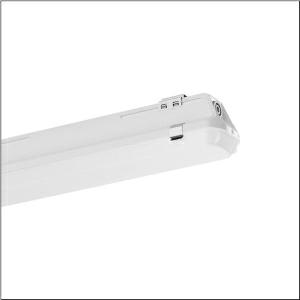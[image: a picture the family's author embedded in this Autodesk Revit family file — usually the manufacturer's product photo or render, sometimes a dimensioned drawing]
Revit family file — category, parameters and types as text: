
# Revit family: monsun_r__21_parking_51fg20dp440bhq_097c
name_source: partatom
category: Lighting Fixtures
units: mm (PartAtom-declared; Revit-internal decimal feet)

## family parameters
Cut with Voids When Loaded = No
Host = Face
Light Source = No
Part Type = Normal
Room Calculation Point = No
Round Connector Dimension = Use Diameter
Shared = No

## types (1)
- --- (1 x LED, 4810 lm, 34.9 W, 4000K)
    Apparent Load = 35 VA
    CIE Flux Codes = 45 75 93 94 100
    Color Rendering = 80
    Color Temperature = 4000K
    Default Elevation = 1800 mm
    Description = Monsun® 21 parking, damp-proof luminaire, chain hanger, primary optical cover: enclosure, of PC, light emission: direct distribution, primary light characteristic: symmetric, installation type: suspended mounting, surface-mounted, horizontal mounting, vertical mounting, LED, rated luminous flux: 4.810lm, luminous efficacy: 140lm/W, light colour: 840, colour temperature: 4000K, control gear: ECG DALI, with terminal, 5-pole, max. 2.5mm², mains connection: 220..240V, AC, 50/60Hz, rated input power: 34W, housing, of glass-fibre reinforced polyester, uncoated, bright grey, incl. chain hanger, length: 1.590mm, width: 90mm, height: 88mm, clip for enclosure, of stainless steel (V2A), ceiling mounting element, of stainless steel (V2A), chain hanger, of stainless steel (V2A), multi-sensor HC1, local controlcentral control, scope of services: certified according to part 101,103,303,304, dimmable, protection rating (complete): IP66, insulation class (complete): insulation class I (protective earthing), certification: CE, ENEC, VDE, UKCA, protection symbol: D, impact resistance: IK08, permissible operating ambient temperature: -25..+35°C, standard: EN 50419, EN 60598-2-1, corresponds to IFS (International Featured Standards) requirements for safety and quality in the food industry, for indoor or canopied outdoor use, no direct snow, no direct sun, no direct rain, contact your sales advisor before using the luminaires in applications with unclear chemical exposure, large temperature fluctuations or condensation-forming humidity, LABS conformity tested according to VDMA 24364:2018-05, packaging unit: 1 piece
    Height = 89 mm
    Lamp = 1 x LED
    Lamp Light Flux = 4810 lm
    Lamp Power = 34.9 W
    Lamp count = 1
    Length = 1590 mm
    Luminous efficacy = 138 lm/W
    Manufacturer = Siteco
    ModVariant = No
    Model = 51FG20DP440BHQ
    Mounting Place = Ceiling
    Mounting Type = Surface mounted
    Number of Poles = 1
    OnlyDefault = Yes
    Power Factor = 1
    Product Name = Monsun® 21 parking
    Product group = damp-proof luminaire
    ProductGroupID = 300
    Protection Class = Protection class I
    Protection Degree = IP 66
    RLX_Detail_Level = 1
    RLX_Emergency_Light_Flux = 0 lm
    RLX_Emergency_Type = 0
    RLX_Emergency_Type_DB = No
    RlxData = <blob elided: 92629 chars, md5=27d10094>
    Socket = socket
    Standby Power = 0 W
    System Light Flux = 4810 lm
    System Power = 35 W
    Type Comments = factory setting: luminous flux: 100 % | dim-lin: 254 | 228 mA
    Type Image = l_1319656.jpg
    URL = http://relux.com
    VarID = @adj_113273
    Voltage = 0 V
    Weight = 0.00 kg
    Width = 90 mm

## geometry (parser evidence)
native form markers: Blend x4, Sweep x12
no freeform markers — native parametric forms only
